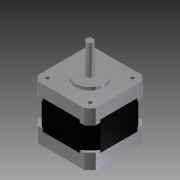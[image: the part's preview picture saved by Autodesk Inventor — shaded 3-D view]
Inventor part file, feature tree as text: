
AUTODESK INVENTOR PART (.ipt)
format: ipt  version: 2013 (Build 170138000, 138)  size: 187,904 bytes
history: native  units: mm
features: sketch x7, extrude x6, hole x1, projected_geometry x1
ambient origin geometry x8: Origin, YZ Plane, XZ Plane, XY Plane, X Axis, Y Axis, Z Axis, Center Point
bodies: Solid1 (feature_tree)
feature tree (15):
  extrude  "Extrusion1"  Depth=54.0mm
  extrude  "Extrusion2"  Depth=11.0mm TaperAngle=0.0deg
  extrude  "Extrusion3"  Depth=0.01mm
  extrude  "Extrusion4"  Depth=9.0mm TaperAngle=0.0deg
  extrude  "Extrusion5"  Depth=2.0mm TaperAngle=0.0deg
  extrude  "Extrusion6"  Depth=22.0mm TaperAngle=0.0deg
  hole  "Hole1"  [1 undecoded]
  sketch  "Sketch1"  dims[d0=42.0mm d1=54.0mm]
  sketch  "Sketch2"  dims[d3=27.0mm d4=11.0mm d5=0.0mm]
  sketch  "Sketch3"  dims[d6=25.0mm d8=0.01mm]
  projected_geometry  "Projected Loop1"
  sketch  "Sketch4"  dims[d9=19.116mm d10=2.0mm d11=0.0mm d12=0.0mm d13=9.0mm d14=2.0mm d15=0.0mm d16=0.0mm]
  sketch  "Sketch5"  dims[d17=22.0mm d19=2.0mm d20=0.0mm]
  sketch  "Sketch6"  dims[d21=5.0mm d23=22.0mm d24=0.0mm]
  sketch  "Sketch7"  dims[d25=2.0mm d26=15.0mm d27=0.0mm d28=31.0mm d29=2.459mm d30=10.0mm d31=4.0mm d32=2.0mm d33=90.0deg d34=10.0mm d35=20.594885mm]
note: 1 required parameter value undecoded (feature->parameter linkage not recoverable at this tier; creation-order binding heuristic only, values carry confidence <= 0.55)
